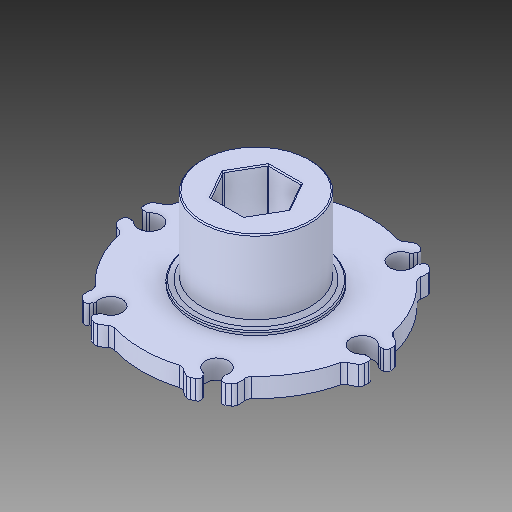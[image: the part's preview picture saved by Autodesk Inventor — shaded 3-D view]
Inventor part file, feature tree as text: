
AUTODESK INVENTOR PART (.ipt)
format: ipt  version: 2019 (Build 230136000, 136)  size: 286,720 bytes
history: native  units: in
note: dims shown in document units (in); Inventor stores cm internally (conversion verified against a paired STEP export)
features: fillet x1
ambient origin geometry x8: Origin, YZ Plane, XZ Plane, XY Plane, X Axis, Y Axis, Z Axis, Center Point
bodies: Solid1 (feature_tree)
feature tree (1):
  fillet  "Fillet7"  [1 undecoded]
note: 1 required parameter value undecoded (feature->parameter linkage not recoverable at this tier; creation-order binding heuristic only, values carry confidence <= 0.55)
